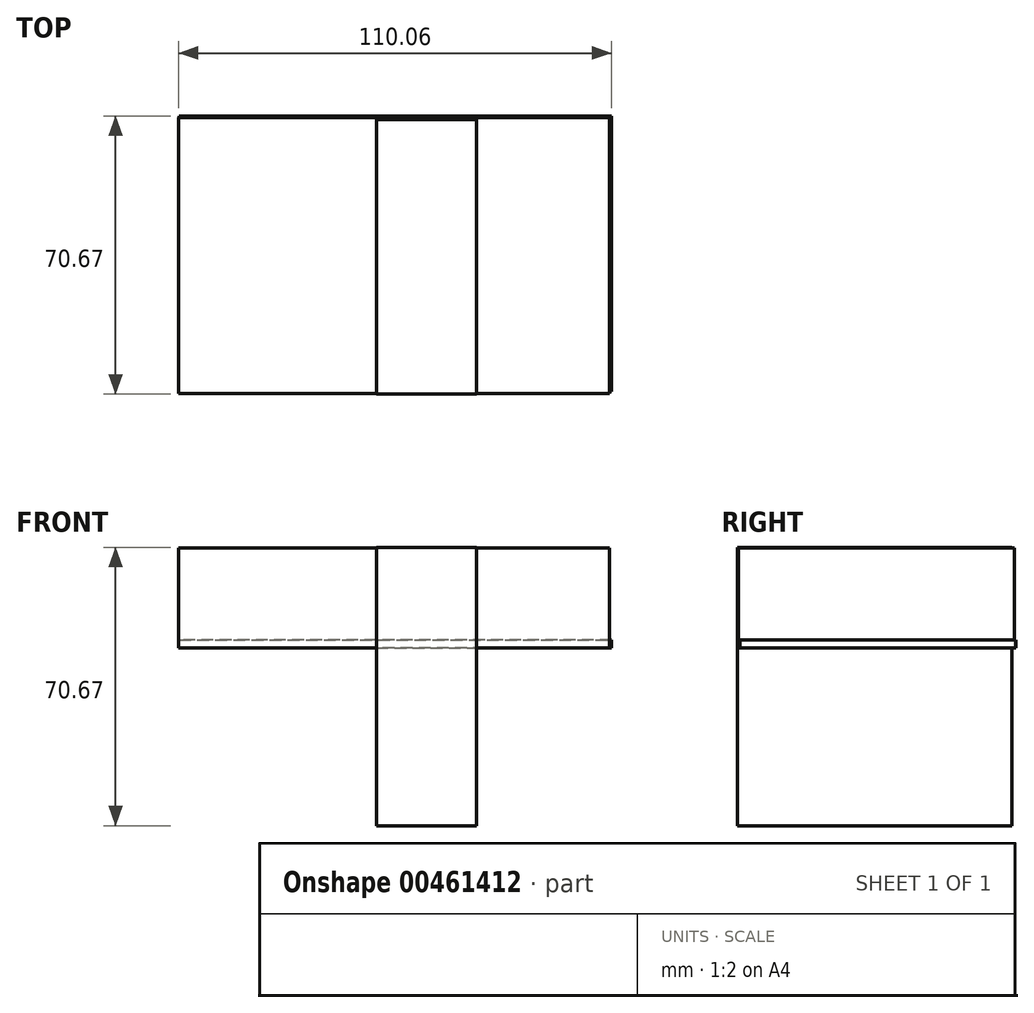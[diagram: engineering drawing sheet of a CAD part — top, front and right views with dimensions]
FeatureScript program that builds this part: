
annotation { "Feature Type Name" : "Feature", "Feature Type Description" : "" }
export const myFeature = defineFeature(function(context is Context, id is Id, definition is map)
    precondition{}
    {
        {
            var Q0;
            Q0=qCreatedBy(makeId("Top.planeOp"),FACE);
            var sketch = newSketch(context, id + "F0", { "sketchPlane" : qUnion([Q0])});
            skLineSegment(sketch, "E0.bottom", {"start": v(-50.29, -28) * mm, "end": v(59.16, -28) * mm});
            skLineSegment(sketch, "E0.top", {"start": v(-50.29, 42.1) * mm, "end": v(59.16, 42.1) * mm});
            skLineSegment(sketch, "E0.left", {"start": v(-50.29, -28) * mm, "end": v(-50.29, 42.1) * mm});
            skLineSegment(sketch, "E0.right", {"start": v(59.16, -28) * mm, "end": v(59.16, 42.1) * mm});
            skSolve(sketch);
        }
        {
            var Q0;
            Q0=makeQuery(id+"F0.imprint","IMPRINT",FACE,{"disambiguationData":[TD([[makeQuery(id+"F0.imprint","IMPRINT",EDGE,{"derivedFrom":sQuery(id+"F0.wireOp",EDGE,"E0.bottom")}),1.0]])]});
            extrude(context, id + "F1", {"entities" : qUnion([Q0]), "depth" : 25.4 * mm});
        }
        {
            var Q0;
            Q0=qCreatedBy(makeId("Right.planeOp"),FACE);
            var sketch = newSketch(context, id + "F2", { "sketchPlane" : qUnion([Q0])});
            skLineSegment(sketch, "E1.bottom", {"start": v(41.56, -45.14) * mm, "end": v(-28.17, -45.14) * mm});
            skLineSegment(sketch, "E1.top", {"start": v(41.56, 25.53) * mm, "end": v(-28.17, 25.53) * mm});
            skLineSegment(sketch, "E1.left", {"start": v(41.56, -45.14) * mm, "end": v(41.56, 25.53) * mm});
            skLineSegment(sketch, "E1.right", {"start": v(-28.17, -45.14) * mm, "end": v(-28.17, 25.53) * mm});
            skSolve(sketch);
        }
        {
            var Q0;
            Q0 = qSketchRegion(id + "F2", true);
            extrude(context, id + "F3", {"entities" : qUnion([Q0]), "operationType" : NewBodyOperationType.ADD, "depth" : 25.4 * mm});
        }
        {
            var Q0;
            Q0=qCreatedBy(makeId("Top.planeOp"),FACE);
            var sketch = newSketch(context, id + "F4", { "sketchPlane" : qUnion([Q0])});
            skLineSegment(sketch, "E2.bottom", {"start": v(59.77, 42.5) * mm, "end": v(-50.12, 42.5) * mm});
            skLineSegment(sketch, "E2.top", {"start": v(59.77, -27.55) * mm, "end": v(-50.12, -27.55) * mm});
            skLineSegment(sketch, "E2.left", {"start": v(59.77, 42.5) * mm, "end": v(59.77, -27.55) * mm});
            skLineSegment(sketch, "E2.right", {"start": v(-50.12, 42.5) * mm, "end": v(-50.12, -27.55) * mm});
            skSolve(sketch);
        }
        {
            var Q0;
            Q0=makeQuery(id+"F4.imprint","IMPRINT",FACE,{"disambiguationData":[TD([[makeQuery(id+"F4.imprint","IMPRINT",EDGE,{"derivedFrom":sQuery(id+"F4.wireOp",EDGE,"E2.bottom")}),1.0]])]});
            extrude(context, id + "F5", {"entities" : qUnion([Q0]), "operationType" : NewBodyOperationType.ADD, "depth" : 2.03 * mm});
        }
    });
